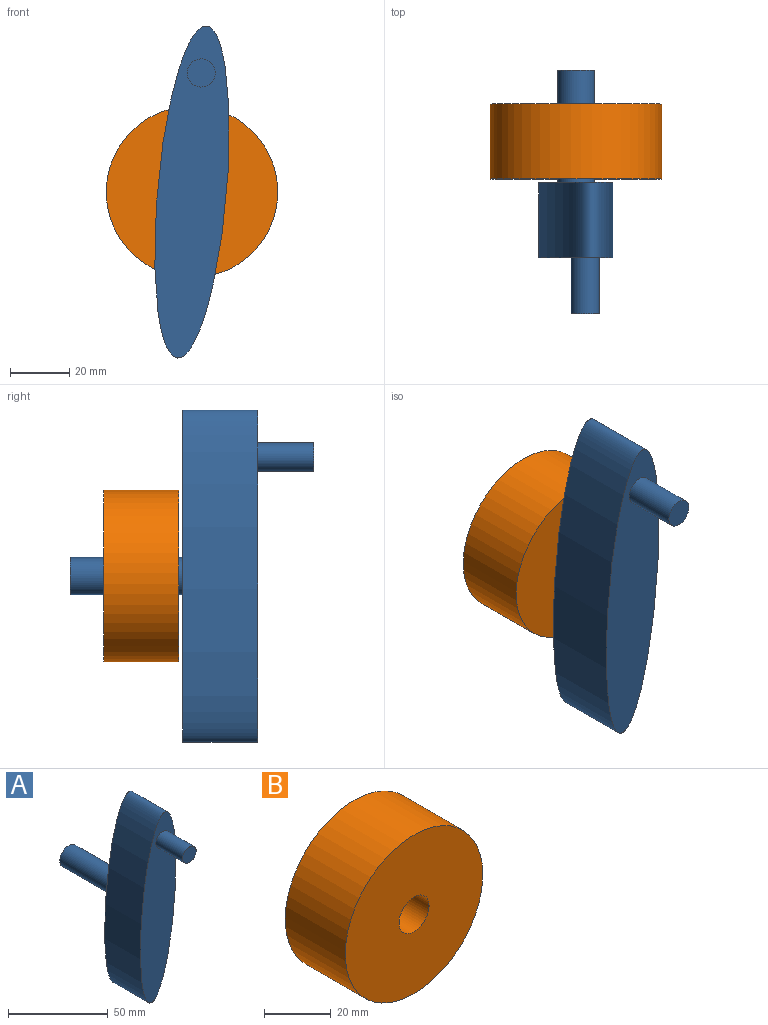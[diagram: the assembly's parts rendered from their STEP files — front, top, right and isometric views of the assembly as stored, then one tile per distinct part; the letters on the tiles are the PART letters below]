
ASSEMBLY  parts=2 mates=1
PART A: 7 faces, bbox 25.3x82.6x112.5 mm
  f0: extruded ~112.47x25.4mm, area 6050.6mm2, adj f1,f2
  f1: plane 112.49x25.31mm, normal (0,-1,0), area 2006.8mm2, adj f0,f5
  f2: plane 112.49x25.31mm, normal (0,1,0), area 1953.9mm2, adj f0,f3
  f3: cylinder r=6.29mm len=38.1mm, axis (0,-1,0), area 1504.9mm2, adj f2,f4
  f4: plane 12.57x12.57mm, normal (0,1,0), area 124.2mm2, adj f3
  f5: cylinder r=4.76mm len=19.05mm, axis (0,1,0), area 570mm2, adj f1,f6
  f6: plane 9.53x9.53mm, normal (0,-1,0), area 71.3mm2, adj f5
PART B: 4 faces, bbox 58.1x25.4x58.1 mm
  f0: cylinder r=29.06mm len=58.11mm, axis (0,1,0), area 4637.3mm2, adj f1,f2
  f1: plane 58.11x58.11mm, normal (0,-1,0), area 2525.8mm2, adj f0,f3
  f2: plane 58.11x58.11mm, normal (0,1,0), area 2525.8mm2, adj f0,f3
  f3: cylinder r=6.35mm len=25.4mm, axis (0,-1,0), area 1013.4mm2, adj f1,f2
PLACE A t=(-50.43,9.68,13.49)mm
PLACE B t=(2.69,36.35,13.49)mm fixed
MATE revolute B.f0 <-> A.f3  axis (0,-1,0) through (-50.43,10.95,13.49)mm
